# Revit family: PKWM_ANG_PSWM_BD
name_source: partatom
category: Lighting Fixtures
units: mm (PartAtom-declared; Revit-internal decimal feet)

## family parameters
Always vertical = Yes
Cut with Voids When Loaded = No
Light Source = No
OmniClass Number = 23.80.70.14
OmniClass Title = Luminaries for External Lighting
Part Type = Normal
Room Calculation Point = No
Round Connector Dimension = Use Diameter
Shared = No
Work Plane-Based = No

## types (13) — shared parameters
Absolute Lumens = 9300 lm
Apparent Load = 57 VA
Assembly Code = D5020200
Base Width = 4.75 "
Description = Exterior Lighting
Frequency = 60 Hz
Full Load Current = 1 A
Glazing Type = Glass-Frosted
Half Base Width = 2.375 "
Half Width = 11 "
Height = 18.375 "
Hood Height = 7.156 "
Lamp = Load Type Catalog for configurations
Manufacturer = Architectural Area Lighting
MasterFormat Number = 26.56.29
MasterFormat Title = Area Lighting
Model = Load Type Catalog for configurations
Mount Width = 8 "
Note Text = LF
Note Visible = Yes
Number of Poles = 1
OmniClass Number = 23.80.70.14.11.17
OmniClass Title = Wall Mounted External Lighting
Power Factor = 1
Series = Period Luminaires
Type Comments = Parkway Square
Voltage = 277 V
Wattage Comments = LU100
Width = 22 "
zero-valued in all types: Default Elevation

## per-type parameters (varying)
| type | Housing Finish | Photometric Web | URL |
| PKWM ANG PSWM-ATG | Aluminum-Antique Green | PKWM : PKWM-ANG-T5-60LED-BW | https://www.currentlighting.com |
| PKWM ANG PSWM-AWT | Aluminum-Artic White | PKWM : PKWM-ANG-T3-60LED-BW | https://www.currentlighting.com |
| PKWM ANG PSWM-BLK | Aluminum-Black | PKWM : PKWM-ANG-T3-60LED-BW | https://www.currentlighting.com |
| PKWM ANG PSWM-MTB | Aluminum-Matte Black | PKWM : PKWM-ANG-T3-60LED-BW | https://www.currentlighting.com |
| PKWM ANG PSWM-DGN | Aluminum-Dark Green | PKWM : PKWM-ANG-T3-60LED-BW | www.aal.nethttps://www.currentlighting.com |
| PKWM ANG PSWM-DBZ | Aluminum-Dark Bronze | PKWM : PKWM-ANG-T3-60LED-BW | https://www.currentlighting.com |
| PKWM ANG PSWM-WRZ | Aluminum-Weathered Bronze | PKWM : PKWM-ANG-T3-60LED-BW | https://www.currentlighting.com |
| PKWM ANG PSWM-BRM | Aluminum-Metalic Bronze | PKWM : PKWM-ANG-Y3HC-32LED-3K-700 | https://www.currentlighting.com |
| PKWM ANG PSWM-VBL | Aluminum-Verde Blue | PKWM : PKWM-ANG-T3-60LED-BW | https://www.currentlighting.com |
| PKWM ANG PSWM-CRT | Aluminum-Corten | PKWM : PKWM-ANG-T3-60LED-BW | https://www.currentlighting.com |
| PKWM ANG PSWM-MAL | Aluminum-Matte | PKWM : PKWM-ANG-T3-60LED-BW | https://www.currentlighting.com |
| PKWM ANG PSWM-MDG | Aluminum-Medium Grey | PKWM : PKWM-ANG-T3-60LED-BW | https://www.currentlighting.com |
| PKWM ANG PSWM-LGY | Aluminum-Light Grey | PKWM : PKWM-ANG-T3-60LED-BW | https://www.currentlighting.com |

## geometry (parser evidence)
native form markers: Blend x30, Sweep x5
no freeform markers — native parametric forms only
